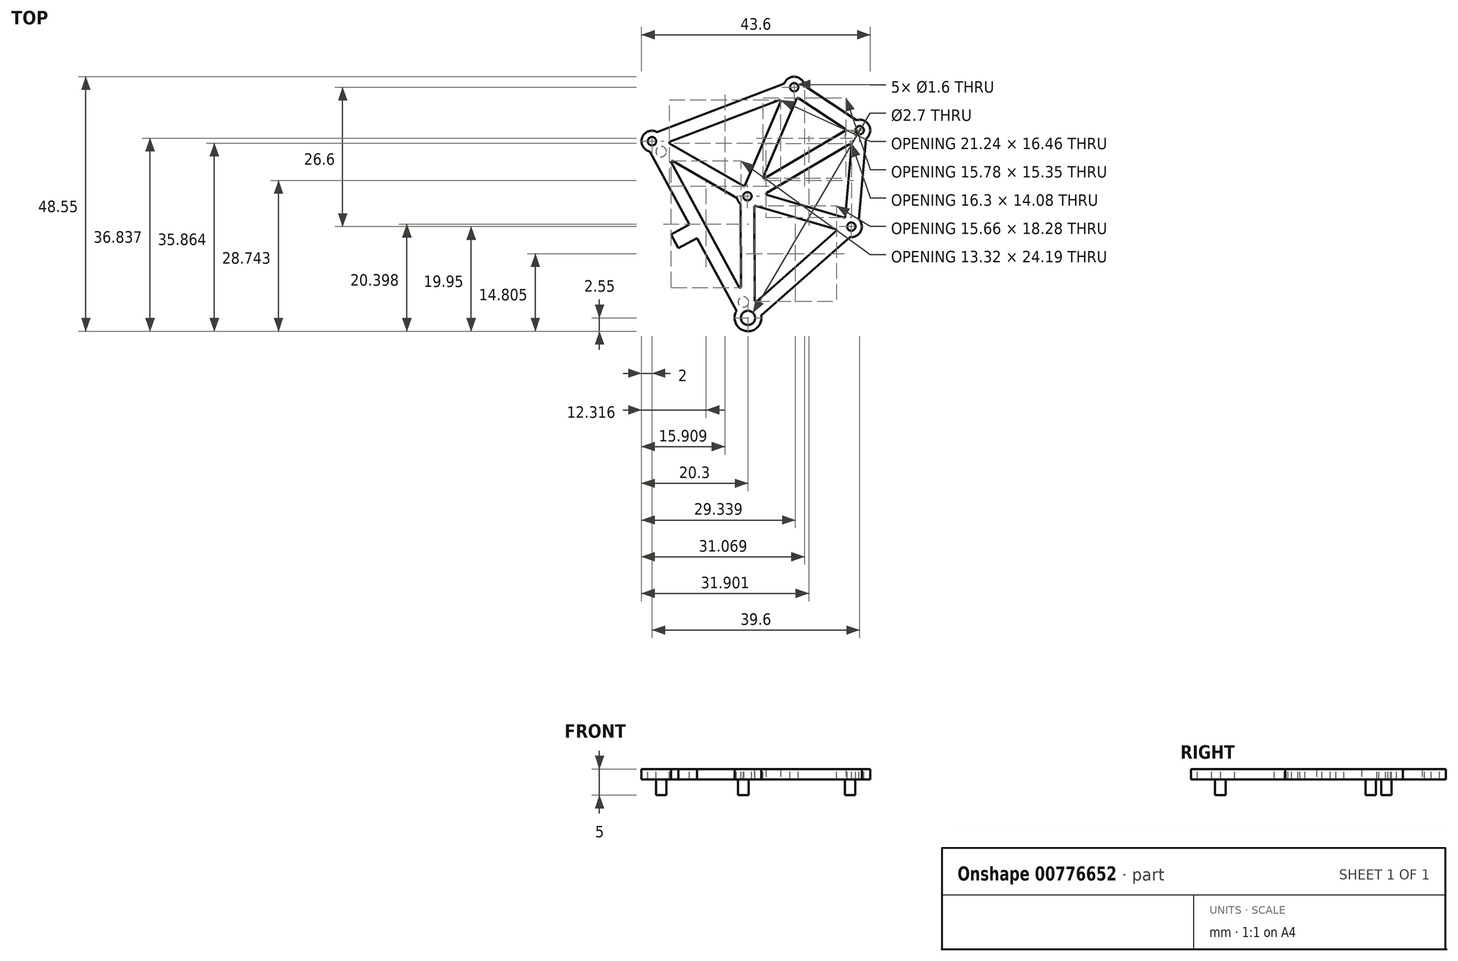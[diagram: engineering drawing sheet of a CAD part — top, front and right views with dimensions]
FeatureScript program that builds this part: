
annotation { "Feature Type Name" : "Feature", "Feature Type Description" : "" }
export const myFeature = defineFeature(function(context is Context, id is Id, definition is map)
    precondition{}
    {
        {
            var Q0;
            Q0=qCreatedBy(makeId("Top.planeOp"),FACE);
            var sketch = newSketch(context, id + "F0", { "sketchPlane" : qUnion([Q0])});
            skCircle(sketch, "E0", {"center": v(4.2, 40) * mm, "radius": 0.8 * mm});
            skCircle(sketch, "E1", {"center": v(31.3, 50.3) * mm, "radius": 0.8 * mm});
            skCircle(sketch, "E2", {"center": v(43.8, 42.1) * mm, "radius": 0.8 * mm});
            skCircle(sketch, "E3", {"center": v(22.4, 29.5) * mm, "radius": 0.8 * mm});
            skCircle(sketch, "E4", {"center": v(22.5, 6.3) * mm, "radius": 1.35 * mm});
            skCircle(sketch, "E5", {"center": v(42.2, 23.7) * mm, "radius": 0.8 * mm});
            skSolve(sketch);
        }
        {
            var Q0;
            Q0=qCreatedBy(makeId("Top.planeOp"),FACE);
            var sketch = newSketch(context, id + "F1", { "sketchPlane" : qUnion([Q0])});
            skCircle(sketch, "E6.0", {"center": v(4.2, 40) * mm, "radius": 0.8 * mm});
            skCircle(sketch, "E7.0", {"center": v(22.4, 29.5) * mm, "radius": 0.8 * mm});
            skCircle(sketch, "E8.0", {"center": v(31.3, 50.3) * mm, "radius": 0.8 * mm});
            skCircle(sketch, "E9.0", {"center": v(43.8, 42.1) * mm, "radius": 0.8 * mm});
            skCircle(sketch, "E10.0", {"center": v(42.2, 23.7) * mm, "radius": 0.8 * mm});
            skCircle(sketch, "E11.0", {"center": v(22.5, 6.3) * mm, "radius": 1.35 * mm});
            skCircle(sketch, "E12", {"center": v(4.2, 40) * mm, "radius": 2 * mm});
            skCircle(sketch, "E13", {"center": v(31.3, 50.3) * mm, "radius": 2 * mm});
            skCircle(sketch, "E14", {"center": v(22.4, 29.5) * mm, "radius": 2 * mm});
            skCircle(sketch, "E15", {"center": v(43.8, 42.1) * mm, "radius": 2 * mm});
            skCircle(sketch, "E16", {"center": v(42.2, 23.7) * mm, "radius": 2 * mm});
            skCircle(sketch, "E17", {"center": v(22.5, 6.3) * mm, "radius": 2.55 * mm});
            skLineSegment(sketch, "E18", {"start": v(5, 40) * mm, "end": v(6.2, 40) * mm, "construction": true});
            skLineSegment(sketch, "E19", {"start": v(23.85, 6.3) * mm, "end": v(25.05, 6.3) * mm, "construction": true});
            skLineSegment(sketch, "E20", {"start": v(4.2, 40) * mm, "end": v(22.5, 6.3) * mm, "construction": true});
            skLineSegment(sketch, "E21", {"start": v(22.5, 6.3) * mm, "end": v(22.4, 29.5) * mm, "construction": true});
            skLineSegment(sketch, "E22", {"start": v(22.4, 29.5) * mm, "end": v(4.2, 40) * mm, "construction": true});
            skLineSegment(sketch, "E23", {"start": v(22.5, 6.3) * mm, "end": v(42.2, 23.7) * mm, "construction": true});
            skLineSegment(sketch, "E24", {"start": v(22.4, 29.5) * mm, "end": v(42.2, 23.7) * mm, "construction": true});
            skLineSegment(sketch, "E25", {"start": v(42.2, 23.7) * mm, "end": v(43.8, 42.1) * mm, "construction": true});
            skLineSegment(sketch, "E26", {"start": v(43.8, 42.1) * mm, "end": v(22.4, 29.5) * mm, "construction": true});
            skLineSegment(sketch, "E27", {"start": v(31.3, 50.3) * mm, "end": v(43.8, 42.1) * mm, "construction": true});
            skLineSegment(sketch, "E28", {"start": v(31.3, 50.3) * mm, "end": v(22.4, 29.5) * mm, "construction": true});
            skLineSegment(sketch, "E29", {"start": v(31.3, 50.3) * mm, "end": v(4.2, 40) * mm, "construction": true});
            skLineSegment(sketch, "E30", {"start": v(29.5, 49.41) * mm, "end": v(21.8, 31.4) * mm});
            skLineSegment(sketch, "E31", {"start": v(25.65, 40.41) * mm, "end": v(28.05, 39.39) * mm, "construction": true});
            skPoint(sketch, "E32", {"position": v(26.85, 39.9) * mm});
            skLineSegment(sketch, "E33", {"start": v(24.2, 30.39) * mm, "end": v(31.9, 48.4) * mm});
            skLineSegment(sketch, "E34", {"start": v(5.16, 41.76) * mm, "end": v(29.42, 50.98) * mm});
            skLineSegment(sketch, "E35", {"start": v(17.29, 46.37) * mm, "end": v(18.21, 43.93) * mm, "construction": true});
            skLineSegment(sketch, "E36", {"start": v(6.08, 39.32) * mm, "end": v(30.34, 48.54) * mm});
            skPoint(sketch, "E37", {"position": v(17.75, 45.15) * mm});
            skLineSegment(sketch, "E38", {"start": v(6.17, 40.37) * mm, "end": v(21.73, 31.39) * mm});
            skLineSegment(sketch, "E39", {"start": v(4.87, 38.11) * mm, "end": v(20.43, 29.13) * mm});
            skLineSegment(sketch, "E40", {"start": v(12.65, 33.62) * mm, "end": v(13.95, 35.88) * mm, "construction": true});
            skPoint(sketch, "E41", {"position": v(13.3, 34.75) * mm});
            skLineSegment(sketch, "E42", {"start": v(23.8, 8.5) * mm, "end": v(23.7, 27.99) * mm});
            skLineSegment(sketch, "E43", {"start": v(21.2, 8.49) * mm, "end": v(21.1, 27.97) * mm});
            skLineSegment(sketch, "E44", {"start": v(21.15, 18.23) * mm, "end": v(23.75, 18.24) * mm, "construction": true});
            skPoint(sketch, "E45", {"position": v(22.45, 18.24) * mm});
            skLineSegment(sketch, "E46", {"start": v(20.31, 7.6) * mm, "end": v(3.78, 38.04) * mm});
            skLineSegment(sketch, "E47", {"start": v(22.6, 8.85) * mm, "end": v(6.07, 39.28) * mm});
            skLineSegment(sketch, "E48", {"start": v(12.05, 22.83) * mm, "end": v(14.33, 24.07) * mm, "construction": true});
            skPoint(sketch, "E49", {"position": v(13.19, 23.45) * mm});
            skLineSegment(sketch, "E50", {"start": v(23.5, 27.83) * mm, "end": v(40.38, 22.88) * mm});
            skLineSegment(sketch, "E51", {"start": v(31.93, 25.35) * mm, "end": v(32.67, 27.85) * mm, "construction": true});
            skPoint(sketch, "E52", {"position": v(32.3, 26.6) * mm});
            skLineSegment(sketch, "E53", {"start": v(41.1, 25.37) * mm, "end": v(24.22, 30.32) * mm});
            skLineSegment(sketch, "E54", {"start": v(25, 6.78) * mm, "end": v(41.92, 21.72) * mm});
            skLineSegment(sketch, "E55", {"start": v(23.28, 8.73) * mm, "end": v(40.2, 23.67) * mm});
            skLineSegment(sketch, "E56", {"start": v(33.46, 14.25) * mm, "end": v(31.74, 16.2) * mm, "construction": true});
            skPoint(sketch, "E57", {"position": v(32.6, 15.22) * mm});
            skLineSegment(sketch, "E58", {"start": v(43.63, 25.1) * mm, "end": v(44.96, 40.47) * mm});
            skLineSegment(sketch, "E59", {"start": v(41.04, 25.33) * mm, "end": v(42.37, 40.7) * mm});
            skLineSegment(sketch, "E60", {"start": v(44.3, 32.79) * mm, "end": v(41.7, 33.01) * mm, "construction": true});
            skPoint(sketch, "E61", {"position": v(43, 32.9) * mm});
            skLineSegment(sketch, "E62", {"start": v(43.24, 44.02) * mm, "end": v(33.28, 50.55) * mm});
            skLineSegment(sketch, "E63", {"start": v(41.82, 41.85) * mm, "end": v(31.86, 48.38) * mm});
            skLineSegment(sketch, "E64", {"start": v(36.84, 45.11) * mm, "end": v(38.26, 47.29) * mm, "construction": true});
            skPoint(sketch, "E65", {"position": v(37.55, 46.2) * mm});
            skLineSegment(sketch, "E66", {"start": v(24.37, 29.15) * mm, "end": v(43.15, 40.2) * mm});
            skLineSegment(sketch, "E67", {"start": v(23.05, 31.4) * mm, "end": v(41.83, 42.45) * mm});
            skLineSegment(sketch, "E68", {"start": v(33.76, 34.68) * mm, "end": v(32.44, 36.92) * mm, "construction": true});
            skPoint(sketch, "E69", {"position": v(33.1, 35.8) * mm});
            skLineSegment(sketch, "E70", {"start": v(11.33, 24.14) * mm, "end": v(7.82, 22.24) * mm});
            skLineSegment(sketch, "E71", {"start": v(7.82, 22.24) * mm, "end": v(9.25, 19.6) * mm});
            skLineSegment(sketch, "E72", {"start": v(9.25, 19.6) * mm, "end": v(12.76, 21.5) * mm});
            skLineSegment(sketch, "E73", {"start": v(12.05, 22.83) * mm, "end": v(8.53, 20.92) * mm, "construction": true});
            skSolve(sketch);
        }
        {
            var Q0;
            {var subQ3=sQuery(id+"F1.wireOp",EDGE,"E34");Q0=makeQuery(id+"F1.imprint","IMPRINT",FACE,{"disambiguationData":[TD([[makeQuery(id+"F1.imprint","IMPRINT",EDGE,{"derivedFrom":subQ3}),-1.0]])]});}
            var Q1;
            {var subQ5=sQuery(id+"F1.wireOp",EDGE,"E62");Q1=makeQuery(id+"F1.imprint","IMPRINT",FACE,{"disambiguationData":[TD([[makeQuery(id+"F1.imprint","IMPRINT",EDGE,{"derivedFrom":subQ5}),1.0]])]});}
            var Q2;
            {var subQ0=sQuery(id+"F1.wireOp",EDGE,"E58");Q2=makeQuery(id+"F1.imprint","IMPRINT",FACE,{"disambiguationData":[TD([[makeQuery(id+"F1.imprint","IMPRINT",EDGE,{"derivedFrom":subQ0}),1.0]])]});}
            var Q3;
            {var subQ9=sQuery(id+"F1.wireOp",EDGE,"E54");Q3=makeQuery(id+"F1.imprint","IMPRINT",FACE,{"disambiguationData":[TD([[makeQuery(id+"F1.imprint","IMPRINT",EDGE,{"derivedFrom":subQ9}),1.0]])]});}
            var Q4;
            Q4=makeQuery(id+"F1.imprint","IMPRINT",FACE,{"disambiguationData":[TD([[makeQuery(id+"F1.imprint","IMPRINT",EDGE,{"derivedFrom":sQuery(id+"F1.wireOp",EDGE,"E6.0")}),-1.0]])]});
            var Q5;
            Q5=makeQuery(id+"F1.imprint","IMPRINT",FACE,{"disambiguationData":[TD([[makeQuery(id+"F1.imprint","IMPRINT",EDGE,{"derivedFrom":sQuery(id+"F1.wireOp",EDGE,"E8.0")}),-1.0]])]});
            var Q6;
            Q6=makeQuery(id+"F1.imprint","IMPRINT",FACE,{"disambiguationData":[TD([[makeQuery(id+"F1.imprint","IMPRINT",EDGE,{"derivedFrom":sQuery(id+"F1.wireOp",EDGE,"E9.0")}),-1.0]])]});
            var Q7;
            Q7=makeQuery(id+"F1.imprint","IMPRINT",FACE,{"disambiguationData":[TD([[makeQuery(id+"F1.imprint","IMPRINT",EDGE,{"derivedFrom":sQuery(id+"F1.wireOp",EDGE,"E10.0")}),-1.0]])]});
            var Q8;
            Q8=makeQuery(id+"F1.imprint","IMPRINT",FACE,{"disambiguationData":[TD([[makeQuery(id+"F1.imprint","IMPRINT",EDGE,{"derivedFrom":sQuery(id+"F1.wireOp",EDGE,"E11.0")}),-1.0]])]});
            var Q9;
            {var subQ3=sQuery(id+"F1.wireOp",EDGE,"E36");var subQ6=sQuery(id+"F1.wireOp",EDGE,"E12");var subQ10=makeQuery(id+"F1.imprint","INTERSECT",VERTEX,{"derivedFrom":[subQ6,subQ3]});Q9=makeQuery(id+"F1.imprint","IMPRINT",FACE,{"disambiguationData":[TD([[makeQuery(id+"F1.imprint","IMPRINT",EDGE,{"disambiguationData":[TD([[subQ10,1.0]])],"derivedFrom":subQ6}),-1.0]])]});}
            var Q10;
            {var subQ0=sQuery(id+"F1.wireOp",EDGE,"E36");var subQ1=sQuery(id+"F1.wireOp",EDGE,"E12");var subQ2=makeQuery(id+"F1.imprint","INTERSECT",VERTEX,{"derivedFrom":[subQ1,subQ0]});Q10=makeQuery(id+"F1.imprint","IMPRINT",FACE,{"disambiguationData":[TD([[makeQuery(id+"F1.imprint","IMPRINT",EDGE,{"disambiguationData":[TD([[subQ2,-1.0]])],"derivedFrom":subQ1}),-1.0]])]});}
            var Q11;
            {var subQ0=sQuery(id+"F1.wireOp",EDGE,"E39");var subQ1=sQuery(id+"F1.wireOp",EDGE,"E12");var subQ2=makeQuery(id+"F1.imprint","INTERSECT",VERTEX,{"derivedFrom":[subQ1,subQ0]});Q11=makeQuery(id+"F1.imprint","IMPRINT",FACE,{"disambiguationData":[TD([[makeQuery(id+"F1.imprint","IMPRINT",EDGE,{"disambiguationData":[TD([[subQ2,-1.0]])],"derivedFrom":subQ1}),-1.0]])]});}
            var Q12;
            {var subQ9=sQuery(id+"F1.wireOp",EDGE,"E46");Q12=makeQuery(id+"F1.imprint","IMPRINT",FACE,{"disambiguationData":[TD([[makeQuery(id+"F1.imprint","IMPRINT",EDGE,{"derivedFrom":subQ9}),-1.0]])]});}
            var Q13;
            {var subQ0=sQuery(id+"F1.wireOp",EDGE,"E43");var subQ1=sQuery(id+"F1.wireOp",EDGE,"E17");var subQ2=makeQuery(id+"F1.imprint","INTERSECT",VERTEX,{"derivedFrom":[subQ1,subQ0]});Q13=makeQuery(id+"F1.imprint","IMPRINT",FACE,{"disambiguationData":[TD([[makeQuery(id+"F1.imprint","IMPRINT",EDGE,{"disambiguationData":[TD([[subQ2,1.0]])],"derivedFrom":subQ1}),-1.0]])]});}
            var Q14;
            {var subQ0=sQuery(id+"F1.wireOp",EDGE,"E42");var subQ1=sQuery(id+"F1.wireOp",EDGE,"E17");var subQ2=makeQuery(id+"F1.imprint","INTERSECT",VERTEX,{"derivedFrom":[subQ1,subQ0]});Q14=makeQuery(id+"F1.imprint","IMPRINT",FACE,{"disambiguationData":[TD([[makeQuery(id+"F1.imprint","IMPRINT",EDGE,{"disambiguationData":[TD([[subQ2,-1.0]])],"derivedFrom":subQ1}),-1.0]])]});}
            var Q15;
            {var subQ0=sQuery(id+"F1.wireOp",EDGE,"E43");var subQ1=sQuery(id+"F1.wireOp",EDGE,"E14");var subQ2=makeQuery(id+"F1.imprint","INTERSECT",VERTEX,{"derivedFrom":[subQ1,subQ0]});Q15=makeQuery(id+"F1.imprint","IMPRINT",FACE,{"disambiguationData":[TD([[makeQuery(id+"F1.imprint","IMPRINT",EDGE,{"disambiguationData":[TD([[subQ2,-1.0]])],"derivedFrom":subQ1}),-1.0]])]});}
            var Q16;
            {var subQ0=sQuery(id+"F1.wireOp",EDGE,"E50");var subQ1=sQuery(id+"F1.wireOp",EDGE,"E16");var subQ2=makeQuery(id+"F1.imprint","INTERSECT",VERTEX,{"derivedFrom":[subQ1,subQ0]});Q16=makeQuery(id+"F1.imprint","IMPRINT",FACE,{"disambiguationData":[TD([[makeQuery(id+"F1.imprint","IMPRINT",EDGE,{"disambiguationData":[TD([[subQ2,1.0]])],"derivedFrom":subQ1}),-1.0]])]});}
            var Q17;
            {var subQ0=sQuery(id+"F1.wireOp",EDGE,"E53");var subQ1=sQuery(id+"F1.wireOp",EDGE,"E16");var subQ2=makeQuery(id+"F1.imprint","INTERSECT",VERTEX,{"derivedFrom":[subQ1,subQ0]});Q17=makeQuery(id+"F1.imprint","IMPRINT",FACE,{"disambiguationData":[TD([[makeQuery(id+"F1.imprint","IMPRINT",EDGE,{"disambiguationData":[TD([[subQ2,-1.0]])],"derivedFrom":subQ1}),-1.0]])]});}
            var Q18;
            {var subQ0=sQuery(id+"F1.wireOp",EDGE,"E30");var subQ1=sQuery(id+"F1.wireOp",EDGE,"E13");var subQ2=makeQuery(id+"F1.imprint","INTERSECT",VERTEX,{"derivedFrom":[subQ1,subQ0]});Q18=makeQuery(id+"F1.imprint","IMPRINT",FACE,{"disambiguationData":[TD([[makeQuery(id+"F1.imprint","IMPRINT",EDGE,{"disambiguationData":[TD([[subQ2,-1.0]])],"derivedFrom":subQ1}),-1.0]])]});}
            var Q19;
            {var subQ0=sQuery(id+"F1.wireOp",EDGE,"E33");var subQ1=sQuery(id+"F1.wireOp",EDGE,"E13");var subQ2=makeQuery(id+"F1.imprint","INTERSECT",VERTEX,{"derivedFrom":[subQ1,subQ0]});Q19=makeQuery(id+"F1.imprint","IMPRINT",FACE,{"disambiguationData":[TD([[makeQuery(id+"F1.imprint","IMPRINT",EDGE,{"disambiguationData":[TD([[subQ2,1.0]])],"derivedFrom":subQ1}),-1.0]])]});}
            var Q20;
            {var subQ0=sQuery(id+"F1.wireOp",EDGE,"E42");var subQ1=sQuery(id+"F1.wireOp",EDGE,"E14");var subQ2=makeQuery(id+"F1.imprint","INTERSECT",VERTEX,{"derivedFrom":[subQ1,subQ0]});Q20=makeQuery(id+"F1.imprint","IMPRINT",FACE,{"disambiguationData":[TD([[makeQuery(id+"F1.imprint","IMPRINT",EDGE,{"disambiguationData":[TD([[subQ2,1.0]])],"derivedFrom":subQ1}),-1.0]])]});}
            var Q21;
            {var subQ8=sQuery(id+"F1.wireOp",EDGE,"E36");var subQ11=sQuery(id+"F1.wireOp",EDGE,"E13");var subQ12=makeQuery(id+"F1.imprint","INTERSECT",VERTEX,{"derivedFrom":[subQ11,subQ8]});Q21=makeQuery(id+"F1.imprint","IMPRINT",FACE,{"disambiguationData":[TD([[makeQuery(id+"F1.imprint","IMPRINT",EDGE,{"disambiguationData":[TD([[subQ12,-1.0]])],"derivedFrom":subQ11}),-1.0]])]});}
            var Q22;
            {var subQ0=sQuery(id+"F1.wireOp",EDGE,"E33");var subQ1=sQuery(id+"F1.wireOp",EDGE,"E14");var subQ2=makeQuery(id+"F1.imprint","INTERSECT",VERTEX,{"derivedFrom":[subQ1,subQ0]});Q22=makeQuery(id+"F1.imprint","IMPRINT",FACE,{"disambiguationData":[TD([[makeQuery(id+"F1.imprint","IMPRINT",EDGE,{"disambiguationData":[TD([[subQ2,-1.0]])],"derivedFrom":subQ1}),-1.0]])]});}
            var Q23;
            Q23=makeQuery(id+"F1.imprint","IMPRINT",FACE,{"disambiguationData":[TD([[makeQuery(id+"F1.imprint","IMPRINT",EDGE,{"derivedFrom":sQuery(id+"F1.wireOp",EDGE,"E7.0")}),-1.0]])]});
            var Q24;
            {var subQ1=sQuery(id+"F1.wireOp",EDGE,"E42");var subQ9=sQuery(id+"F1.wireOp",EDGE,"E14");var subQ10=makeQuery(id+"F1.imprint","INTERSECT",VERTEX,{"derivedFrom":[subQ9,subQ1]});Q24=makeQuery(id+"F1.imprint","IMPRINT",FACE,{"disambiguationData":[TD([[makeQuery(id+"F1.imprint","IMPRINT",EDGE,{"disambiguationData":[TD([[subQ10,-1.0]])],"derivedFrom":subQ9}),-1.0]])]});}
            var Q25;
            {var subQ0=sQuery(id+"F1.wireOp",EDGE,"E53");var subQ1=sQuery(id+"F1.wireOp",EDGE,"E14");var subQ2=makeQuery(id+"F1.imprint","INTERSECT",VERTEX,{"derivedFrom":[subQ1,subQ0]});Q25=makeQuery(id+"F1.imprint","IMPRINT",FACE,{"disambiguationData":[TD([[makeQuery(id+"F1.imprint","IMPRINT",EDGE,{"disambiguationData":[TD([[subQ2,1.0]])],"derivedFrom":subQ1}),-1.0]])]});}
            var Q26;
            {var subQ6=sQuery(id+"F1.wireOp",EDGE,"E14");var subQ10=sQuery(id+"F1.wireOp",EDGE,"E33");var subQ11=makeQuery(id+"F1.imprint","INTERSECT",VERTEX,{"derivedFrom":[subQ6,subQ10]});Q26=makeQuery(id+"F1.imprint","IMPRINT",FACE,{"disambiguationData":[TD([[makeQuery(id+"F1.imprint","IMPRINT",EDGE,{"disambiguationData":[TD([[subQ11,1.0]])],"derivedFrom":subQ6}),-1.0]])]});}
            var Q27;
            {var subQ0=sQuery(id+"F1.wireOp",EDGE,"E63");var subQ1=sQuery(id+"F1.wireOp",EDGE,"E15");var subQ2=makeQuery(id+"F1.imprint","INTERSECT",VERTEX,{"derivedFrom":[subQ1,subQ0]});Q27=makeQuery(id+"F1.imprint","IMPRINT",FACE,{"disambiguationData":[TD([[makeQuery(id+"F1.imprint","IMPRINT",EDGE,{"disambiguationData":[TD([[subQ2,1.0]])],"derivedFrom":subQ1}),-1.0]])]});}
            var Q28;
            {var subQ0=sQuery(id+"F1.wireOp",EDGE,"E59");var subQ1=sQuery(id+"F1.wireOp",EDGE,"E15");var subQ2=makeQuery(id+"F1.imprint","INTERSECT",VERTEX,{"derivedFrom":[subQ1,subQ0]});Q28=makeQuery(id+"F1.imprint","IMPRINT",FACE,{"disambiguationData":[TD([[makeQuery(id+"F1.imprint","IMPRINT",EDGE,{"disambiguationData":[TD([[subQ2,-1.0]])],"derivedFrom":subQ1}),-1.0]])]});}
            var Q29;
            {var subQ0=sQuery(id+"F1.wireOp",EDGE,"E70");Q29=makeQuery(id+"F1.imprint","IMPRINT",FACE,{"disambiguationData":[TD([[makeQuery(id+"F1.imprint","IMPRINT",EDGE,{"derivedFrom":subQ0}),1.0]])]});}
            extrude(context, id + "F2", {"entities" : qUnion([Q0, Q1, Q2, Q3, Q4, Q5, Q6, Q7, Q8, Q9, Q10, Q11, Q12, Q13, Q14, Q15, Q16, Q17, Q18, Q19, Q20, Q21, Q22, Q23, Q24, Q25, Q26, Q27, Q28, Q29]), "oppositeDirection" : true, "depth" : 2 * mm, "offsetDistance" : 25 * mm});
        }
        {
            var Q0;
            Q0=makeQuery(id+"F2.opExtrude","CAP_FACE",FACE,{"disambiguationData":[OSD([sQuery(id+"F1.wireOp",EDGE,"E6.0"),sQuery(id+"F1.wireOp",EDGE,"E7.0"),sQuery(id+"F1.wireOp",EDGE,"E8.0"),sQuery(id+"F1.wireOp",EDGE,"E9.0"),sQuery(id+"F1.wireOp",EDGE,"E10.0"),sQuery(id+"F1.wireOp",EDGE,"E11.0"),sQuery(id+"F1.wireOp",EDGE,"E12"),sQuery(id+"F1.wireOp",EDGE,"E13"),sQuery(id+"F1.wireOp",EDGE,"E14"),sQuery(id+"F1.wireOp",EDGE,"E15"),sQuery(id+"F1.wireOp",EDGE,"E16"),sQuery(id+"F1.wireOp",EDGE,"E17"),sQuery(id+"F1.wireOp",EDGE,"E30"),sQuery(id+"F1.wireOp",EDGE,"E33"),sQuery(id+"F1.wireOp",EDGE,"E34"),sQuery(id+"F1.wireOp",EDGE,"E36"),sQuery(id+"F1.wireOp",EDGE,"E38"),sQuery(id+"F1.wireOp",EDGE,"E39"),sQuery(id+"F1.wireOp",EDGE,"E42"),sQuery(id+"F1.wireOp",EDGE,"E43"),sQuery(id+"F1.wireOp",EDGE,"E46"),sQuery(id+"F1.wireOp",EDGE,"E47"),sQuery(id+"F1.wireOp",EDGE,"E50"),sQuery(id+"F1.wireOp",EDGE,"E53"),sQuery(id+"F1.wireOp",EDGE,"E54"),sQuery(id+"F1.wireOp",EDGE,"E55"),sQuery(id+"F1.wireOp",EDGE,"E58"),sQuery(id+"F1.wireOp",EDGE,"E59"),sQuery(id+"F1.wireOp",EDGE,"E62"),sQuery(id+"F1.wireOp",EDGE,"E63"),sQuery(id+"F1.wireOp",EDGE,"E66"),sQuery(id+"F1.wireOp",EDGE,"E67")])],"isStart":true});
            var sketch = newSketch(context, id + "F3", { "sketchPlane" : qUnion([Q0])});
            skCircle(sketch, "E74", {"center": v(21.62, 9.34) * mm, "radius": 1 * mm});
            skCircle(sketch, "E75", {"center": v(41.96, 40.99) * mm, "radius": 1 * mm});
            skCircle(sketch, "E76", {"center": v(5.94, 38.02) * mm, "radius": 1 * mm});
            skLineSegment(sketch, "E77", {"start": v(3.78, 38.04) * mm, "end": v(5.94, 38.02) * mm, "construction": true});
            skLineSegment(sketch, "E78", {"start": v(5.94, 38.02) * mm, "end": v(7.22, 39.76) * mm, "construction": true});
            skLineSegment(sketch, "E79", {"start": v(5.94, 38.02) * mm, "end": v(7.54, 36.57) * mm, "construction": true});
            skLineSegment(sketch, "E80", {"start": v(41.34, 42.16) * mm, "end": v(41.96, 40.99) * mm, "construction": true});
            skLineSegment(sketch, "E81", {"start": v(41.96, 40.99) * mm, "end": v(42.29, 39.7) * mm, "construction": true});
            skLineSegment(sketch, "E82", {"start": v(41.96, 40.99) * mm, "end": v(43.8, 42.1) * mm, "construction": true});
            skLineSegment(sketch, "E83", {"start": v(21.18, 11.46) * mm, "end": v(21.62, 9.34) * mm, "construction": true});
            skLineSegment(sketch, "E84", {"start": v(23.79, 9.17) * mm, "end": v(21.62, 9.34) * mm, "construction": true});
            skLineSegment(sketch, "E85", {"start": v(21.62, 9.34) * mm, "end": v(20.31, 7.6) * mm, "construction": true});
            skSolve(sketch);
        }
        {
            var Q0;
            Q0=makeQuery(id+"F3.imprint","IMPRINT",FACE,{"disambiguationData":[TD([[makeQuery(id+"F3.imprint","IMPRINT",EDGE,{"derivedFrom":sQuery(id+"F3.wireOp",EDGE,"E74")}),1.0]])]});
            var Q1;
            Q1=makeQuery(id+"F3.imprint","IMPRINT",FACE,{"disambiguationData":[TD([[makeQuery(id+"F3.imprint","IMPRINT",EDGE,{"derivedFrom":sQuery(id+"F3.wireOp",EDGE,"E76")}),1.0]])]});
            var Q2;
            Q2=makeQuery(id+"F3.imprint","IMPRINT",FACE,{"disambiguationData":[TD([[makeQuery(id+"F3.imprint","IMPRINT",EDGE,{"derivedFrom":sQuery(id+"F3.wireOp",EDGE,"E75")}),1.0]])]});
            extrude(context, id + "F4", {"entities" : qUnion([Q0, Q1, Q2]), "operationType" : NewBodyOperationType.ADD, "oppositeDirection" : true, "depth" : 5 * mm, "offsetDistance" : 25 * mm});
        }
        {
            var Q0;
            Q0=makeQuery(id+"F2.opExtrude","SWEPT_EDGE",EDGE,{"disambiguationData":[OSD([sQuery(id+"F1.wireOp",EDGE,"E36"),sQuery(id+"F1.wireOp",EDGE,"E38")])]});
            var Q1;
            Q1=makeQuery(id+"F2.opExtrude","SWEPT_EDGE",EDGE,{"disambiguationData":[OSD([sQuery(id+"F1.wireOp",EDGE,"E39"),sQuery(id+"F1.wireOp",EDGE,"E47")])]});
            var Q2;
            Q2=makeQuery(id+"F2.opExtrude","SWEPT_EDGE",EDGE,{"disambiguationData":[OSD([sQuery(id+"F1.wireOp",EDGE,"E43"),sQuery(id+"F1.wireOp",EDGE,"E47")])]});
            var Q3;
            Q3=makeQuery(id+"F2.opExtrude","SWEPT_EDGE",EDGE,{"disambiguationData":[OSD([sQuery(id+"F1.wireOp",EDGE,"E42"),sQuery(id+"F1.wireOp",EDGE,"E55")])]});
            var Q4;
            Q4=makeQuery(id+"F2.opExtrude","SWEPT_EDGE",EDGE,{"disambiguationData":[OSD([sQuery(id+"F1.wireOp",EDGE,"E17"),sQuery(id+"F1.wireOp",EDGE,"E46")])]});
            var Q5;
            Q5=makeQuery(id+"F2.opExtrude","SWEPT_EDGE",EDGE,{"disambiguationData":[OSD([sQuery(id+"F1.wireOp",EDGE,"E17"),sQuery(id+"F1.wireOp",EDGE,"E54")])]});
            var Q6;
            Q6=makeQuery(id+"F2.opExtrude","SWEPT_EDGE",EDGE,{"disambiguationData":[OSD([sQuery(id+"F1.wireOp",EDGE,"E14"),sQuery(id+"F1.wireOp",EDGE,"E43")])]});
            var Q7;
            Q7=makeQuery(id+"F2.opExtrude","SWEPT_EDGE",EDGE,{"disambiguationData":[OSD([sQuery(id+"F1.wireOp",EDGE,"E14"),sQuery(id+"F1.wireOp",EDGE,"E39")])]});
            var Q8;
            Q8=makeQuery(id+"F2.opExtrude","SWEPT_EDGE",EDGE,{"disambiguationData":[OSD([sQuery(id+"F1.wireOp",EDGE,"E12"),sQuery(id+"F1.wireOp",EDGE,"E46")])]});
            var Q9;
            Q9=makeQuery(id+"F2.opExtrude","SWEPT_EDGE",EDGE,{"disambiguationData":[OSD([sQuery(id+"F1.wireOp",EDGE,"E12"),sQuery(id+"F1.wireOp",EDGE,"E34")])]});
            var Q10;
            Q10=makeQuery(id+"F2.opExtrude","SWEPT_EDGE",EDGE,{"disambiguationData":[OSD([sQuery(id+"F1.wireOp",EDGE,"E13"),sQuery(id+"F1.wireOp",EDGE,"E34")])]});
            var Q11;
            Q11=makeQuery(id+"F2.opExtrude","SWEPT_EDGE",EDGE,{"disambiguationData":[OSD([sQuery(id+"F1.wireOp",EDGE,"E30"),sQuery(id+"F1.wireOp",EDGE,"E36")])]});
            var Q12;
            Q12=makeQuery(id+"F2.opExtrude","SWEPT_EDGE",EDGE,{"disambiguationData":[OSD([sQuery(id+"F1.wireOp",EDGE,"E33"),sQuery(id+"F1.wireOp",EDGE,"E63")])]});
            var Q13;
            Q13=makeQuery(id+"F2.opExtrude","SWEPT_EDGE",EDGE,{"disambiguationData":[OSD([sQuery(id+"F1.wireOp",EDGE,"E13"),sQuery(id+"F1.wireOp",EDGE,"E62")])]});
            var Q14;
            Q14=makeQuery(id+"F2.opExtrude","SWEPT_EDGE",EDGE,{"disambiguationData":[OSD([sQuery(id+"F1.wireOp",EDGE,"E15"),sQuery(id+"F1.wireOp",EDGE,"E62")])]});
            var Q15;
            Q15=makeQuery(id+"F2.opExtrude","SWEPT_EDGE",EDGE,{"disambiguationData":[OSD([sQuery(id+"F1.wireOp",EDGE,"E15"),sQuery(id+"F1.wireOp",EDGE,"E58")])]});
            var Q16;
            Q16=makeQuery(id+"F2.opExtrude","SWEPT_EDGE",EDGE,{"disambiguationData":[OSD([sQuery(id+"F1.wireOp",EDGE,"E59"),sQuery(id+"F1.wireOp",EDGE,"E66")])]});
            var Q17;
            Q17=makeQuery(id+"F2.opExtrude","SWEPT_EDGE",EDGE,{"disambiguationData":[OSD([sQuery(id+"F1.wireOp",EDGE,"E63"),sQuery(id+"F1.wireOp",EDGE,"E67")])]});
            var Q18;
            Q18=makeQuery(id+"F2.opExtrude","SWEPT_EDGE",EDGE,{"disambiguationData":[OSD([sQuery(id+"F1.wireOp",EDGE,"E16"),sQuery(id+"F1.wireOp",EDGE,"E58")])]});
            var Q19;
            Q19=makeQuery(id+"F2.opExtrude","SWEPT_EDGE",EDGE,{"disambiguationData":[OSD([sQuery(id+"F1.wireOp",EDGE,"E16"),sQuery(id+"F1.wireOp",EDGE,"E54")])]});
            var Q20;
            Q20=makeQuery(id+"F2.opExtrude","SWEPT_EDGE",EDGE,{"disambiguationData":[OSD([sQuery(id+"F1.wireOp",EDGE,"E50"),sQuery(id+"F1.wireOp",EDGE,"E55")])]});
            var Q21;
            Q21=makeQuery(id+"F2.opExtrude","SWEPT_EDGE",EDGE,{"disambiguationData":[OSD([sQuery(id+"F1.wireOp",EDGE,"E53"),sQuery(id+"F1.wireOp",EDGE,"E59")])]});
            var Q22;
            Q22=makeQuery(id+"F2.opExtrude","SWEPT_EDGE",EDGE,{"disambiguationData":[OSD([sQuery(id+"F1.wireOp",EDGE,"E14"),sQuery(id+"F1.wireOp",EDGE,"E30")])]});
            var Q23;
            Q23=makeQuery(id+"F2.opExtrude","SWEPT_EDGE",EDGE,{"disambiguationData":[OSD([sQuery(id+"F1.wireOp",EDGE,"E33"),sQuery(id+"F1.wireOp",EDGE,"E67")])]});
            var Q24;
            Q24=makeQuery(id+"F2.opExtrude","SWEPT_EDGE",EDGE,{"disambiguationData":[OSD([sQuery(id+"F1.wireOp",EDGE,"E53"),sQuery(id+"F1.wireOp",EDGE,"E66")])]});
            var Q25;
            Q25=makeQuery(id+"F2.opExtrude","SWEPT_EDGE",EDGE,{"disambiguationData":[OSD([sQuery(id+"F1.wireOp",EDGE,"E42"),sQuery(id+"F1.wireOp",EDGE,"E50")])]});
            fillet(context, id + "F5", {"entities" : qUnion([Q0, Q1, Q2, Q3, Q4, Q5, Q6, Q7, Q8, Q9, Q10, Q11, Q12, Q13, Q14, Q15, Q16, Q17, Q18, Q19, Q20, Q21, Q22, Q23, Q24, Q25]), "radius" : 0.2 * mm, "tangentPropagation" : true, "allowEdgeOverflow" : false});
        }
    });
